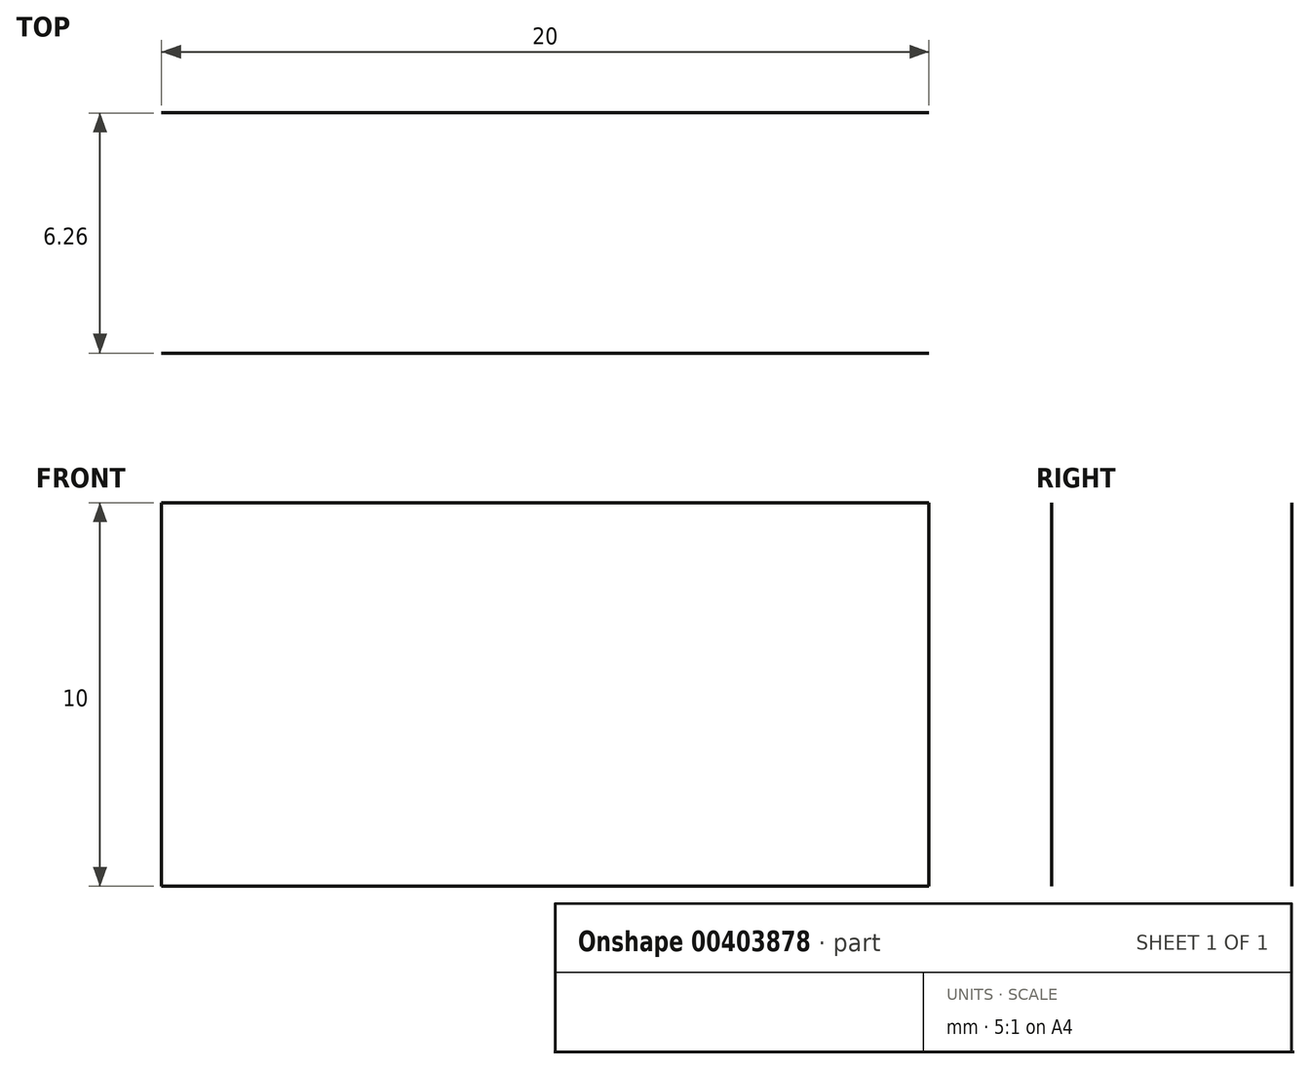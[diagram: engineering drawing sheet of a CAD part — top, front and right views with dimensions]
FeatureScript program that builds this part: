
annotation { "Feature Type Name" : "Feature", "Feature Type Description" : "" }
export const myFeature = defineFeature(function(context is Context, id is Id, definition is map)
    precondition{}
    {
        {
            var Q0;
            Q0=qCreatedBy(makeId("Top.planeOp"),FACE);
            var sketch = newSketch(context, id + "F0", { "sketchPlane" : qUnion([Q0])});
            skLineSegment(sketch, "E0.bottom", {"start": v(10, 0) * mm, "end": v(-10, 0) * mm});
            skLineSegment(sketch, "E0.top", {"start": v(10, 6.26) * mm, "end": v(-10, 6.26) * mm});
            skLineSegment(sketch, "E0.left", {"start": v(10, 0) * mm, "end": v(10, 6.26) * mm});
            skLineSegment(sketch, "E0.right", {"start": v(-10, 0) * mm, "end": v(-10, 6.26) * mm});
            skPoint(sketch, "E0.middle", {"position": v(0, 3.13) * mm});
            skSolve(sketch);
        }
        {
            var Q0;
            Q0=sQuery(id+"F0.wireOp",EDGE,"E0.top");
            var Q1;
            Q1=sQuery(id+"F0.wireOp",EDGE,"E0.bottom");
            extrude(context, id + "F1", {"bodyType" : ToolBodyType.SURFACE, "surfaceEntities" : qUnion([Q0, Q1]), "depth" : 10 * mm});
        }
    });
